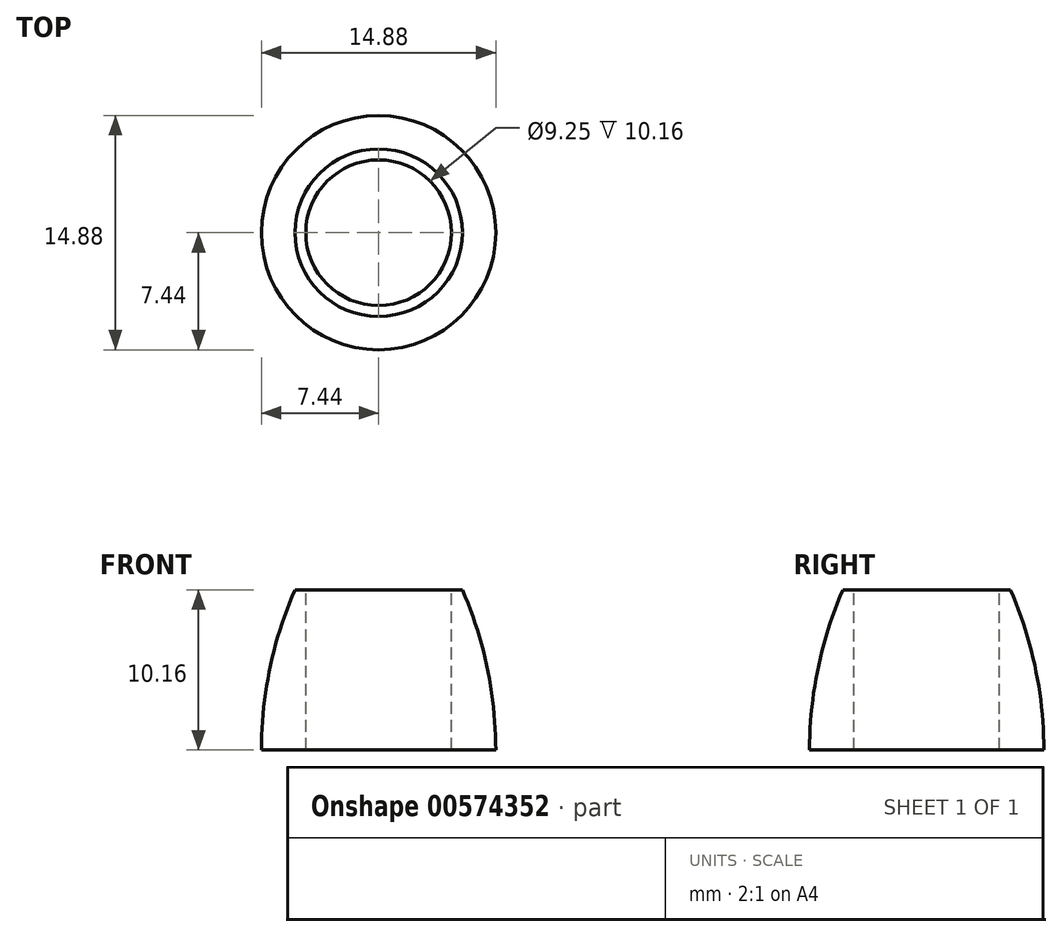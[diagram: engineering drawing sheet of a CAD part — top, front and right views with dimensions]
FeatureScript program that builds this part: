
annotation { "Feature Type Name" : "Feature", "Feature Type Description" : "" }
export const myFeature = defineFeature(function(context is Context, id is Id, definition is map)
    precondition{}
    {
        {
            var Q0;
            Q0=qCreatedBy(makeId("Front.planeOp"),FACE);
            var sketch = newSketch(context, id + "F0", { "sketchPlane" : qUnion([Q0])});
            skCircle(sketch, "E0", {"center": v(-17.96, 0) * mm, "radius": 25.4 * mm, "construction": true});
            skLineSegment(sketch, "E1", {"start": v(0, 17.96) * mm, "end": v(0, -17.96) * mm, "construction": true});
            skLineSegment(sketch, "E2", {"start": v(-17.96, 0) * mm, "end": v(0, 17.96) * mm, "construction": true});
            skLineSegment(sketch, "E3", {"start": v(0, -17.96) * mm, "end": v(-17.96, 0) * mm, "construction": true});
            skLineSegment(sketch, "E4", {"start": v(5.32, 10.16) * mm, "end": v(4.62, 10.16) * mm});
            skLineSegment(sketch, "E5", {"start": v(4.62, 10.16) * mm, "end": v(4.62, -10.16) * mm});
            skLineSegment(sketch, "E6", {"start": v(4.62, -10.16) * mm, "end": v(5.32, -10.16) * mm});
            skArc(sketch, "E7", {"start": v(5.32, -10.16) * mm, "mid": v(7.44, 0) * mm, "end": v(5.32, 10.16) * mm});
            skLineSegment(sketch, "E8", {"start": v(4.62, 0) * mm, "end": v(7.44, 0) * mm});
            skSolve(sketch);
        }
        {
            var Q0;
            {var subQ0=sQuery(id+"F0.wireOp",EDGE,"E4");Q0=makeQuery(id+"F0.imprint","IMPRINT",FACE,{"disambiguationData":[TD([[makeQuery(id+"F0.imprint","IMPRINT",EDGE,{"derivedFrom":subQ0}),1.0]])]});}
            var Q1;
            Q1=sQuery(id+"F0.wireOp",EDGE,"E1");
            revolve(context, id + "F1", {"surfaceOperationType" : NewSurfaceOperationType.NEW, "entities" : qUnion([Q0]), "axis" : qUnion([Q1]), "revolveType" : RevolveType.FULL});
        }
    });
